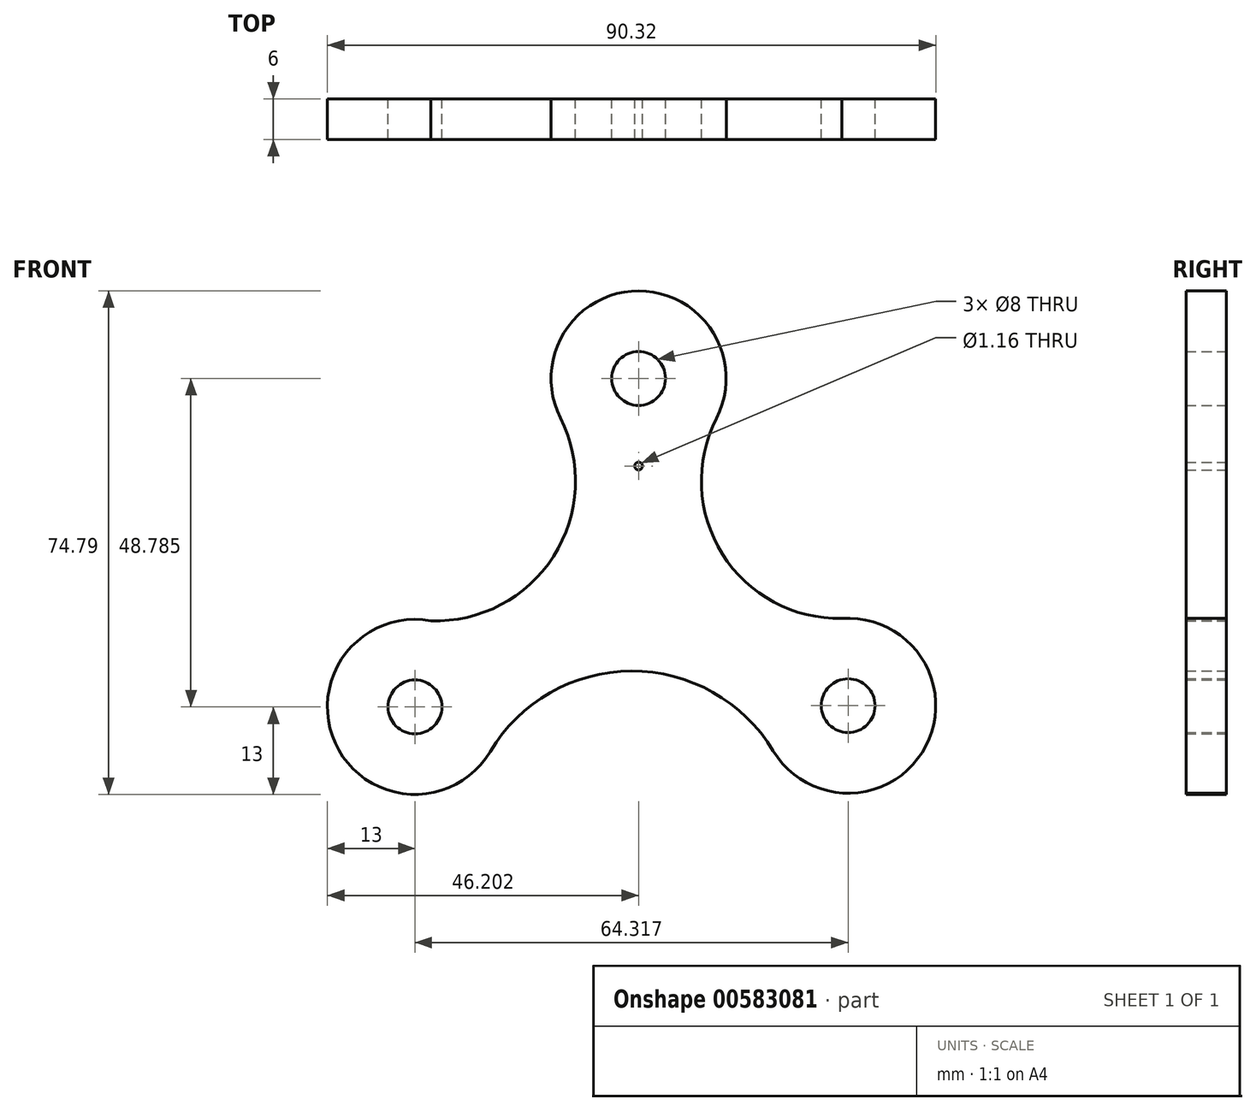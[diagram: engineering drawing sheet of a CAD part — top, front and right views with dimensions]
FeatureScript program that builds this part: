
annotation { "Feature Type Name" : "Feature", "Feature Type Description" : "" }
export const myFeature = defineFeature(function(context is Context, id is Id, definition is map)
    precondition{}
    {
        {
            var Q0;
            Q0=qCreatedBy(makeId("Front.planeOp"),FACE);
            var sketch = newSketch(context, id + "F0", { "sketchPlane" : qUnion([Q0])});
            skCircle(sketch, "E0", {"center": v(0, 0) * mm, "radius": 13 * mm});
            skCircle(sketch, "E1", {"center": v(64.32, 0.19) * mm, "radius": 13 * mm});
            skCircle(sketch, "E2", {"center": v(33.2, 48.79) * mm, "radius": 13 * mm});
            skCircle(sketch, "E3", {"center": v(33.2, 18.31) * mm, "radius": 13 * mm});
            skArc(sketch, "E4", {"start": v(0, 13) * mm, "mid": v(19.9, 21.39) * mm, "end": v(21.6, 42.92) * mm});
            skArc(sketch, "E5", {"start": v(44.77, 42.86) * mm, "mid": v(45.64, 22.71) * mm, "end": v(63.4, 13.15) * mm});
            skArc(sketch, "E6", {"start": v(53.18, -6.52) * mm, "mid": v(32.14, 5.33) * mm, "end": v(11.17, -6.64) * mm});
            skCircle(sketch, "E7", {"center": v(33.2, 35.79) * mm, "radius": 0.58 * mm});
            skCircle(sketch, "E8", {"center": v(33.2, 48.79) * mm, "radius": 9.5 * mm});
            skCircle(sketch, "E9", {"center": v(33.2, 48.79) * mm, "radius": 4 * mm});
            skCircle(sketch, "E10", {"center": v(0, 0) * mm, "radius": 9.5 * mm});
            skCircle(sketch, "E11", {"center": v(0, 0) * mm, "radius": 4 * mm});
            skCircle(sketch, "E12", {"center": v(64.32, 0.19) * mm, "radius": 9.5 * mm});
            skCircle(sketch, "E13", {"center": v(64.32, 0.19) * mm, "radius": 4 * mm});
            skSolve(sketch);
        }
        {
            var Q0;
            Q0 = qSketchRegion(id + "F0", true);
            var Q1;
            Q1=makeQuery(id+"F0.imprint","IMPRINT",FACE,{"disambiguationData":[TD([[makeQuery(id+"F0.imprint","IMPRINT",EDGE,{"derivedFrom":sQuery(id+"F0.wireOp",EDGE,"E8")}),1.0]])]});
            var Q2;
            Q2=makeQuery(id+"F0.imprint","IMPRINT",FACE,{"disambiguationData":[TD([[makeQuery(id+"F0.imprint","IMPRINT",EDGE,{"derivedFrom":sQuery(id+"F0.wireOp",EDGE,"E10")}),1.0]])]});
            var Q3;
            Q3=makeQuery(id+"F0.imprint","IMPRINT",FACE,{"disambiguationData":[TD([[makeQuery(id+"F0.imprint","IMPRINT",EDGE,{"derivedFrom":sQuery(id+"F0.wireOp",EDGE,"E12")}),1.0]])]});
            extrude(context, id + "F1", {"entities" : qUnion([Q0, Q1, Q2, Q3]), "depth" : 6 * mm, "offsetDistance" : 25 * mm});
        }
    });
